AUTODESK INVENTOR PART (.ipt)
format: ipt  version: 2021 (Build 250183000, 183)  size: 601,600 bytes
history: native  units: mm
features: other x8, sketch x4, projected_geometry x2, hole x1
ambient origin geometry x8: Origin, YZ Plane, XZ Plane, XY Plane, X Axis, Y Axis, Z Axis, Center Point
bodies: Body1 (feature_tree)
feature tree (15):
  other  "外殼件底.ipt"
  sketch  "草圖1"
  hole  "孔1"  [1 undecoded]
  other  "實體7::外殼件底.ipt"
  other  "標籤特徵1"
  sketch  "草圖2"
  projected_geometry  "投影迴路1"
  other  "平板1"
  other  "實體2"
  sketch  "草圖4"
  projected_geometry  "投影迴路2"
  other  "平板2"
  other  "折彎2"
  sketch  "草圖5"
  other  "實體1"
note: 1 required parameter value undecoded (feature->parameter linkage not recoverable at this tier; creation-order binding heuristic only, values carry confidence <= 0.55)
